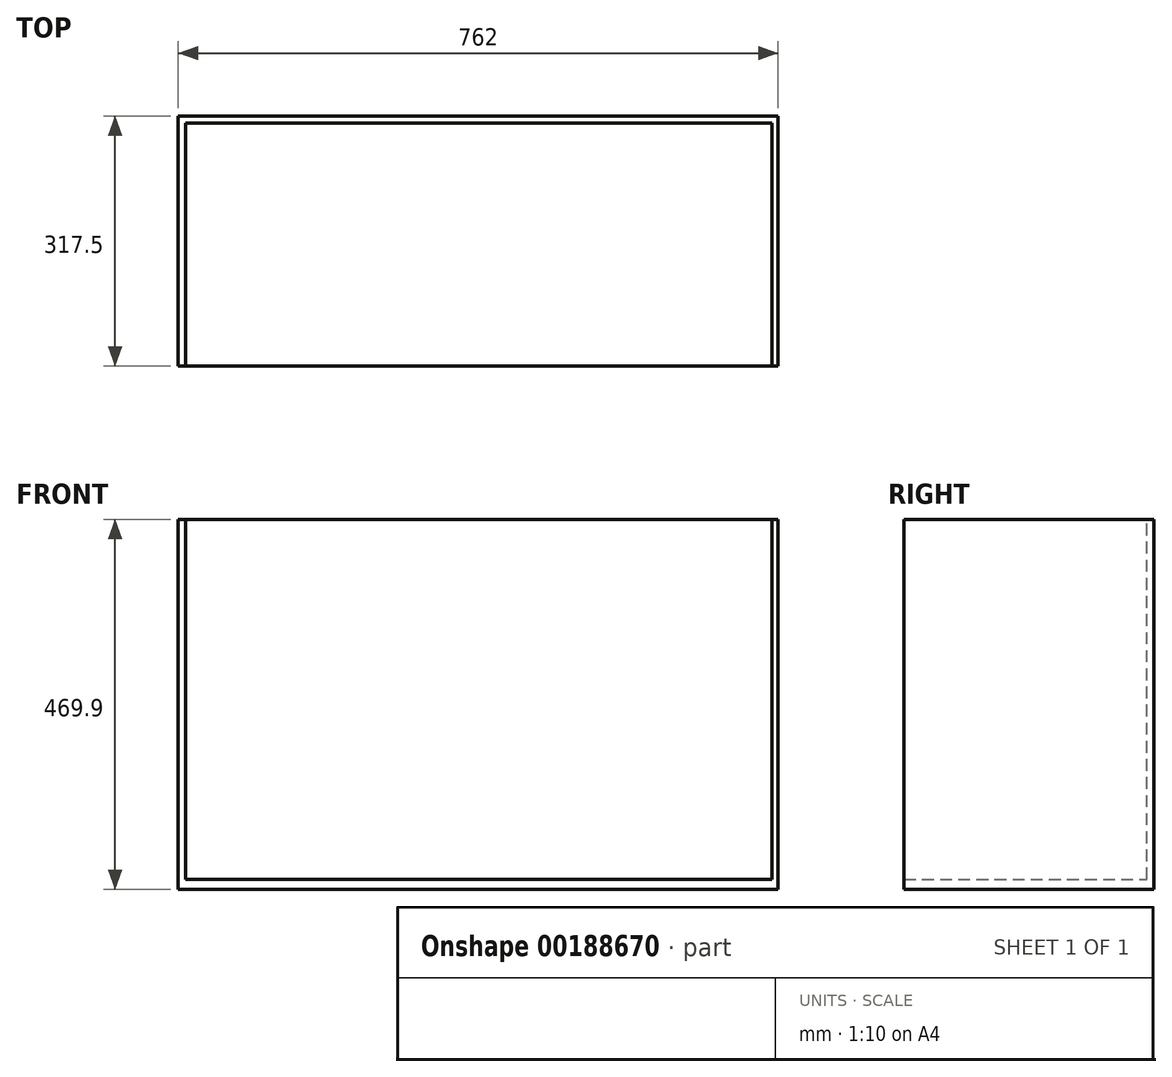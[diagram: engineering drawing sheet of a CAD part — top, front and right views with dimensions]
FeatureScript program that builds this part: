
annotation { "Feature Type Name" : "Feature", "Feature Type Description" : "" }
export const myFeature = defineFeature(function(context is Context, id is Id, definition is map)
    precondition{}
    {
        {
            var Q0;
            Q0=qCreatedBy(makeId("Top.planeOp"),FACE);
            var sketch = newSketch(context, id + "F0", { "sketchPlane" : qUnion([Q0])});
            skLineSegment(sketch, "E0.bottom", {"start": v(-401.7, 0) * mm, "end": v(360.3, 0) * mm});
            skLineSegment(sketch, "E0.top", {"start": v(-401.7, -317.5) * mm, "end": v(360.3, -317.5) * mm});
            skLineSegment(sketch, "E0.left", {"start": v(-401.7, 0) * mm, "end": v(-401.7, -317.5) * mm});
            skLineSegment(sketch, "E0.right", {"start": v(360.3, 0) * mm, "end": v(360.3, -317.5) * mm});
            skSolve(sketch);
        }
        {
            var Q0;
            Q0=makeQuery(id+"F0.imprint","IMPRINT",FACE,{"disambiguationData":[TD([[makeQuery(id+"F0.imprint","IMPRINT",EDGE,{"derivedFrom":sQuery(id+"F0.wireOp",EDGE,"E0.bottom")}),-1.0]])]});
            extrude(context, id + "F1", {"entities" : qUnion([Q0]), "oppositeDirection" : true, "depth" : 469.9 * mm});
        }
        {
            var Q0;
            Q0=makeQuery(id+"F1.opExtrude","CAP_FACE",FACE,{"disambiguationData":[OSD([sQuery(id+"F0.wireOp",EDGE,"E0.bottom"),sQuery(id+"F0.wireOp",EDGE,"E0.top"),sQuery(id+"F0.wireOp",EDGE,"E0.left"),sQuery(id+"F0.wireOp",EDGE,"E0.right")])],"isStart":true});
            var sketch = newSketch(context, id + "F2", { "sketchPlane" : qUnion([Q0])});
            skLineSegment(sketch, "E1.bottom", {"start": v(-392.5, -317.5) * mm, "end": v(352.23, -317.5) * mm});
            skLineSegment(sketch, "E1.top", {"start": v(-392.5, -9.04) * mm, "end": v(352.23, -9.04) * mm});
            skLineSegment(sketch, "E1.left", {"start": v(-392.5, -317.5) * mm, "end": v(-392.5, -9.04) * mm});
            skLineSegment(sketch, "E1.right", {"start": v(352.23, -317.5) * mm, "end": v(352.23, -9.04) * mm});
            skSolve(sketch);
        }
        {
            var Q0;
            Q0 = qSketchRegion(id + "F2", true);
            extrude(context, id + "F3", {"entities" : qUnion([Q0]), "operationType" : NewBodyOperationType.REMOVE, "oppositeDirection" : true, "depth" : 457.2 * mm});
        }
    });
